# Revit family: TataSteel_Lintels_CH_90-105_125-140
name_source: partatom
category: Generic Models
revit_build: Autodesk Revit 2015 (Build: 20140606_1530(x64)
units: mm (PartAtom-declared; Revit-internal decimal feet)

## types (1)
- TataSteel_Lintels_CH_90-105_125-140
    AllowableLoadLimiting = 31 mm  [stored 0.101706 ft]
    AssetType = FIXED
    BIMObjectName = TataSteel_Lintel_CHB90_125_3000
    BIMobject category = Beams & Lintels
    CharacteristicDeflectionUnderLoad = 0 mm  [stored 0 ft]
    CharacteristicResistanceToFire = 60 mm  [stored 0.19685 ft]
    CharacteristicThermalConductivity = 0 mm  [stored 0 ft]
    Color = Black
    Date of publishing = 7/15/2016
    Description = Heavy duty cavity wall lintel
    Edition number = 1
    ExpectedLife = 60 yrs
    Finish = Galv and Powder coated
    FireRating = 60
    Grade = DX51
    IFC Classification = Structural Member
    IfcExportAs = IfcBeamType
    IfcExportType = LINTEL
    Installation instructions = http://catnic.com
    InstallationDate = 1900-12-31T23:59:59
    Insulation = Steel
    IsExternal = Yes
    LengthIncrement = 150mm up to 3000mm. 
300mm above 3000mm
    LintelCavity = 88 mm  [stored 0.288714 ft]
    LintelHeight = 158 mm
    LintelInnerLeaf = 125 mm  [stored 0.410105 ft]
    LintelLength = 3000 mm  [stored 9.84252 ft]
    LintelOuterLeaf = 95 mm
    LintelPlateThickness = 2 mm  [stored 0.00656168 ft]
    LintelPlateWidth = 152 mm  [stored 0.498688 ft]
    LintelThickness = 3 mm  [stored 0.00984252 ft]
    LintelTopFlange1 = 51 mm
    LintelTopFlange2 = 48 mm  [stored 0.15748 ft]
    LintelType = CAVITY
    LoadBearing = Yes
    LoadCategory = HEAVY DUTY
    Manufacturer = Catnic, TATA
    Manufacturer country = United Kingdom
    Manufacturer name = Tata Steel
    ManufacturerURL = www.catnic.com
    Material = Galvanised Steel
    Material main = Steel
    MaxLintelLength = 2400
    MinLintelLength = 900
    Model = TataSteel_Lintel_CHB90_125_3000
    ModelNumber = CH
    ModelReference = Cavity Walls
    NBSDescription = Pre fabricated Steel Lintel
    NBSReference = F30 755
    Name = Lintel
    Nominal height = 0
    Nominal width = 0
    NominalLength = 3000 mm  [stored 9.84252 ft]
    OmniClass Code = 23-13 21 25 11
    OmniClass Description = Lintels
    Product Guid = 15f34378-b20d-4e1e-b467-f7dc8f1ee97b
    Product SKU = catnic-ch
    Product certification = http://catnic.com
    Product family = Lintels
    Product group = Catnic
    ProductInformation = www.catnic.com
    QR code = http://bimobject.com
    Roll = 0 mm  [stored 0 ft]
    SafeWorkingLoad = 31 mm  [stored 0.101706 ft]
    Shape = Open back lintel
    Size = 158H x315W x3000L
    Slope = 0 mm  [stored 0 ft]
    Span = 2700 mm  [stored 8.85827 ft]
    Steel = Steel
    TSE_BIMObjectName = TataSteel_Lintel_CHB90_125_3000
    TSE_Documentation = www.catnic.com
    TSE_InstallationInstructions = www.catnic.com
    TSE_ManufacturerURL = www.catnic.com
    TSE_Model = TataSteel_Lintel_CHB90_125_3000
    TSE_ProductCertification = www.catnic.com
    TSE_QR code = <None>
    Technical description = http://catnic.com
    ThermalTransmittance = 0 mm  [stored 0 ft]
    UNSPSC Code = 30101704
    URL = www.catnic.com
    Uniclass 1.4 Code = L3241
    Uniclass 1.4 Description = Lintels
    Uniclass 2015 Code = Pr_20_85_48
    Uniclass 2015 Name = Lintels
    Uniclass2015 = Pr_20_85_48_11
    WallCavityRange = 90-105
    WallInnerLeafRange = 125-140
    WarrantyStartDate = 1900-12-31T23:59:59
    Weight = 14 mm  [stored 0.0459318 ft]
    Weight Net (Kg) = 0
    b1 = 139 mm  [stored 0.456037 ft]
    b2 = 169 mm
    b3 = 44 mm  [stored 0.144357 ft]
    b5 = 2 mm  [stored 0.00656168 ft]
    b6 = 76 mm  [stored 0.249344 ft]

note: [stored X ft] marks values corroborated as IEEE doubles in the binary element streams (Revit-internal decimal feet)

## geometry (parser evidence)
native form markers: Sweep x3
no freeform markers — native parametric forms only
